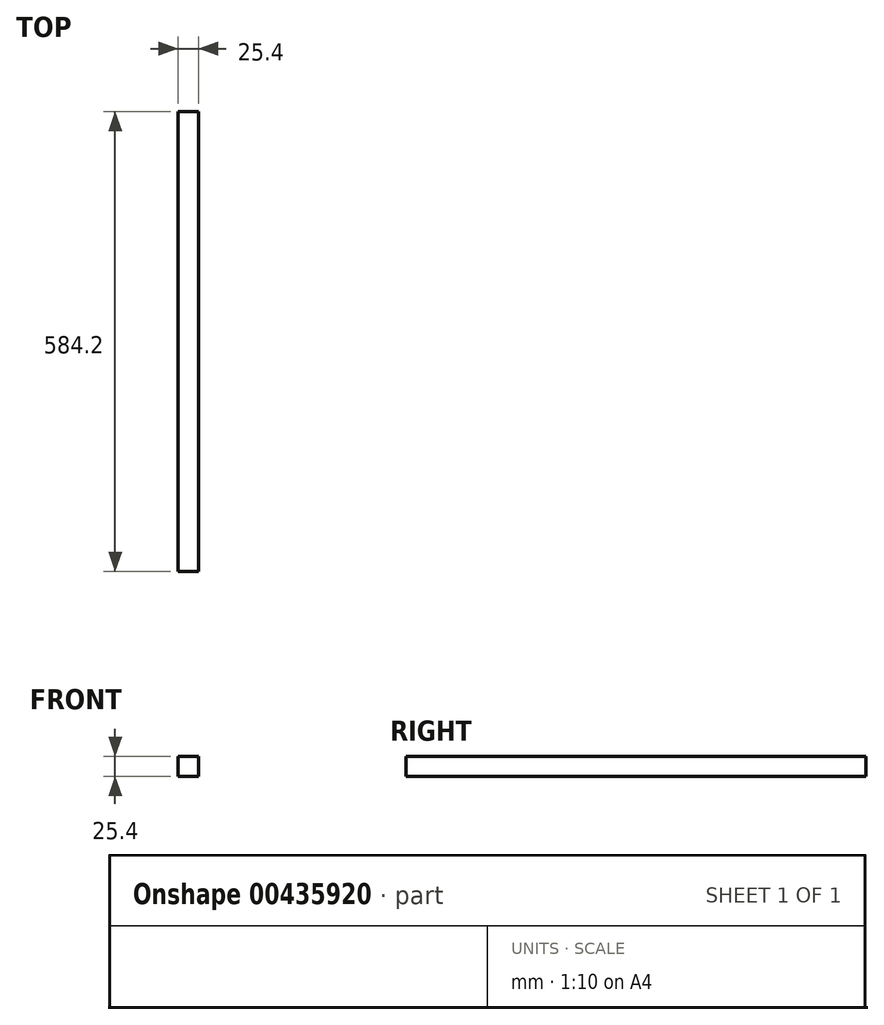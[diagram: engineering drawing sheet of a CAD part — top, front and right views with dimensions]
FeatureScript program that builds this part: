
annotation { "Feature Type Name" : "Feature", "Feature Type Description" : "" }
export const myFeature = defineFeature(function(context is Context, id is Id, definition is map)
    precondition{}
    {
        {
            var Q0;
            Q0=qCreatedBy(makeId("Front.planeOp"),FACE);
            var sketch = newSketch(context, id + "F0", { "sketchPlane" : qUnion([Q0])});
            skLineSegment(sketch, "E0.bottom", {"start": v(-12.7, 12.7) * mm, "end": v(12.7, 12.7) * mm});
            skLineSegment(sketch, "E0.top", {"start": v(-12.7, -12.7) * mm, "end": v(12.7, -12.7) * mm});
            skLineSegment(sketch, "E0.left", {"start": v(-12.7, 12.7) * mm, "end": v(-12.7, -12.7) * mm});
            skLineSegment(sketch, "E0.right", {"start": v(12.7, 12.7) * mm, "end": v(12.7, -12.7) * mm});
            skPoint(sketch, "E0.middle", {"position": v(0, 0) * mm});
            skSolve(sketch);
        }
        {
            var Q0;
            Q0 = qSketchRegion(id + "F0", true);
            extrude(context, id + "F1", {"entities" : qUnion([Q0]), "depth" : 584.2 * mm});
        }
    });
